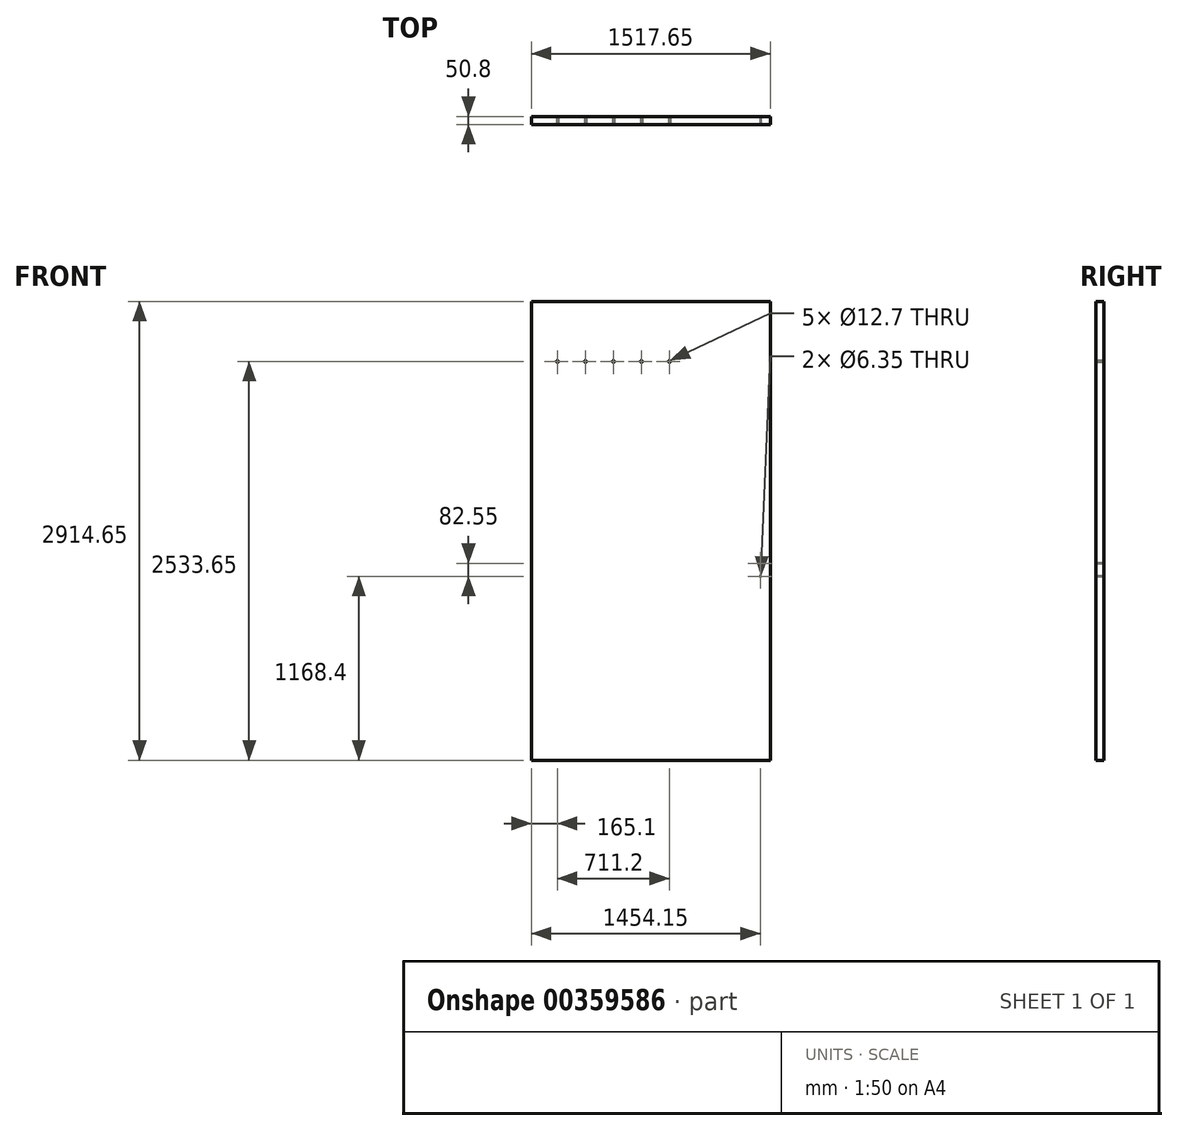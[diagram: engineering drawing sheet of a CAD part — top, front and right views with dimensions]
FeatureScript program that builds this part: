
annotation { "Feature Type Name" : "Feature", "Feature Type Description" : "" }
export const myFeature = defineFeature(function(context is Context, id is Id, definition is map)
    precondition{}
    {
        {
            var Q0;
            Q0=qCreatedBy(makeId("Front.planeOp"),FACE);
            var sketch = newSketch(context, id + "F0", { "sketchPlane" : qUnion([Q0])});
            skLineSegment(sketch, "E0.bottom", {"start": v(0, 0) * mm, "end": v(1517.65, 0) * mm});
            skLineSegment(sketch, "E0.top", {"start": v(0, 2914.65) * mm, "end": v(1517.65, 2914.65) * mm});
            skLineSegment(sketch, "E0.left", {"start": v(0, 0) * mm, "end": v(0, 2914.65) * mm});
            skLineSegment(sketch, "E0.right", {"start": v(1517.65, 0) * mm, "end": v(1517.65, 2914.65) * mm});
            skSolve(sketch);
        }
        {
            var Q0;
            Q0=makeQuery(id+"F0.imprint","IMPRINT",FACE,{"disambiguationData":[TD([[makeQuery(id+"F0.imprint","IMPRINT",EDGE,{"derivedFrom":sQuery(id+"F0.wireOp",EDGE,"E0.bottom")}),1.0]])]});
            extrude(context, id + "F1", {"entities" : qUnion([Q0]), "depth" : 50.8 * mm});
        }
        {
            var Q0;
            Q0=makeQuery(id+"F1.opExtrude","CAP_FACE",FACE,{"disambiguationData":[OSD([sQuery(id+"F0.wireOp",EDGE,"E0.bottom"),sQuery(id+"F0.wireOp",EDGE,"E0.top"),sQuery(id+"F0.wireOp",EDGE,"E0.left"),sQuery(id+"F0.wireOp",EDGE,"E0.right")])],"isStart":false});
            var sketch = newSketch(context, id + "F2", { "sketchPlane" : qUnion([Q0])});
            skLineSegment(sketch, "E1", {"start": v(-490.58, 2533.65) * mm, "end": v(1934.23, 2533.65) * mm, "construction": true});
            skPoint(sketch, "E2", {"position": v(165.1, 2533.65) * mm});
            skCircle(sketch, "E3", {"center": v(165.1, 2533.65) * mm, "radius": 6.35 * mm});
            skCircle(sketch, "E4.1.0.0", {"center": v(342.9, 2533.65) * mm, "radius": 6.35 * mm});
            skCircle(sketch, "E4.2.0.0", {"center": v(520.7, 2533.65) * mm, "radius": 6.35 * mm});
            skCircle(sketch, "E4.3.0.0", {"center": v(698.5, 2533.65) * mm, "radius": 6.35 * mm});
            skCircle(sketch, "E4.4.0.0", {"center": v(876.3, 2533.65) * mm, "radius": 6.35 * mm});
            skLineSegment(sketch, "E4.direction1", {"start": v(165.1, 2533.65) * mm, "end": v(342.9, 2533.65) * mm, "construction": true});
            skSolve(sketch);
        }
        {
            var Q0;
            Q0 = qSketchRegion(id + "F2", true);
            extrude(context, id + "F3", {"entities" : qUnion([Q0]), "operationType" : NewBodyOperationType.REMOVE, "endBound" : BoundingType.THROUGH_ALL, "oppositeDirection" : true, "depth" : 25.4 * mm});
        }
        {
            var Q0;
            Q0=makeQuery(id+"F1.opExtrude","CAP_FACE",FACE,{"disambiguationData":[OSD([sQuery(id+"F0.wireOp",EDGE,"E0.bottom"),sQuery(id+"F0.wireOp",EDGE,"E0.top"),sQuery(id+"F0.wireOp",EDGE,"E0.left"),sQuery(id+"F0.wireOp",EDGE,"E0.right")])],"isStart":false});
            var sketch = newSketch(context, id + "F4", { "sketchPlane" : qUnion([Q0])});
            skCircle(sketch, "E5", {"center": v(1454.15, 1250.95) * mm, "radius": 3.18 * mm});
            skCircle(sketch, "E6", {"center": v(1454.15, 1168.4) * mm, "radius": 3.18 * mm});
            skLineSegment(sketch, "E7", {"start": v(1454.15, 1165.9) * mm, "end": v(1454.15, 1201.9) * mm, "construction": true});
            skSolve(sketch);
        }
        {
            var Q0;
            Q0 = qSketchRegion(id + "F4", true);
            extrude(context, id + "F5", {"entities" : qUnion([Q0]), "operationType" : NewBodyOperationType.REMOVE, "endBound" : BoundingType.THROUGH_ALL, "oppositeDirection" : true, "depth" : 25.4 * mm});
        }
    });
